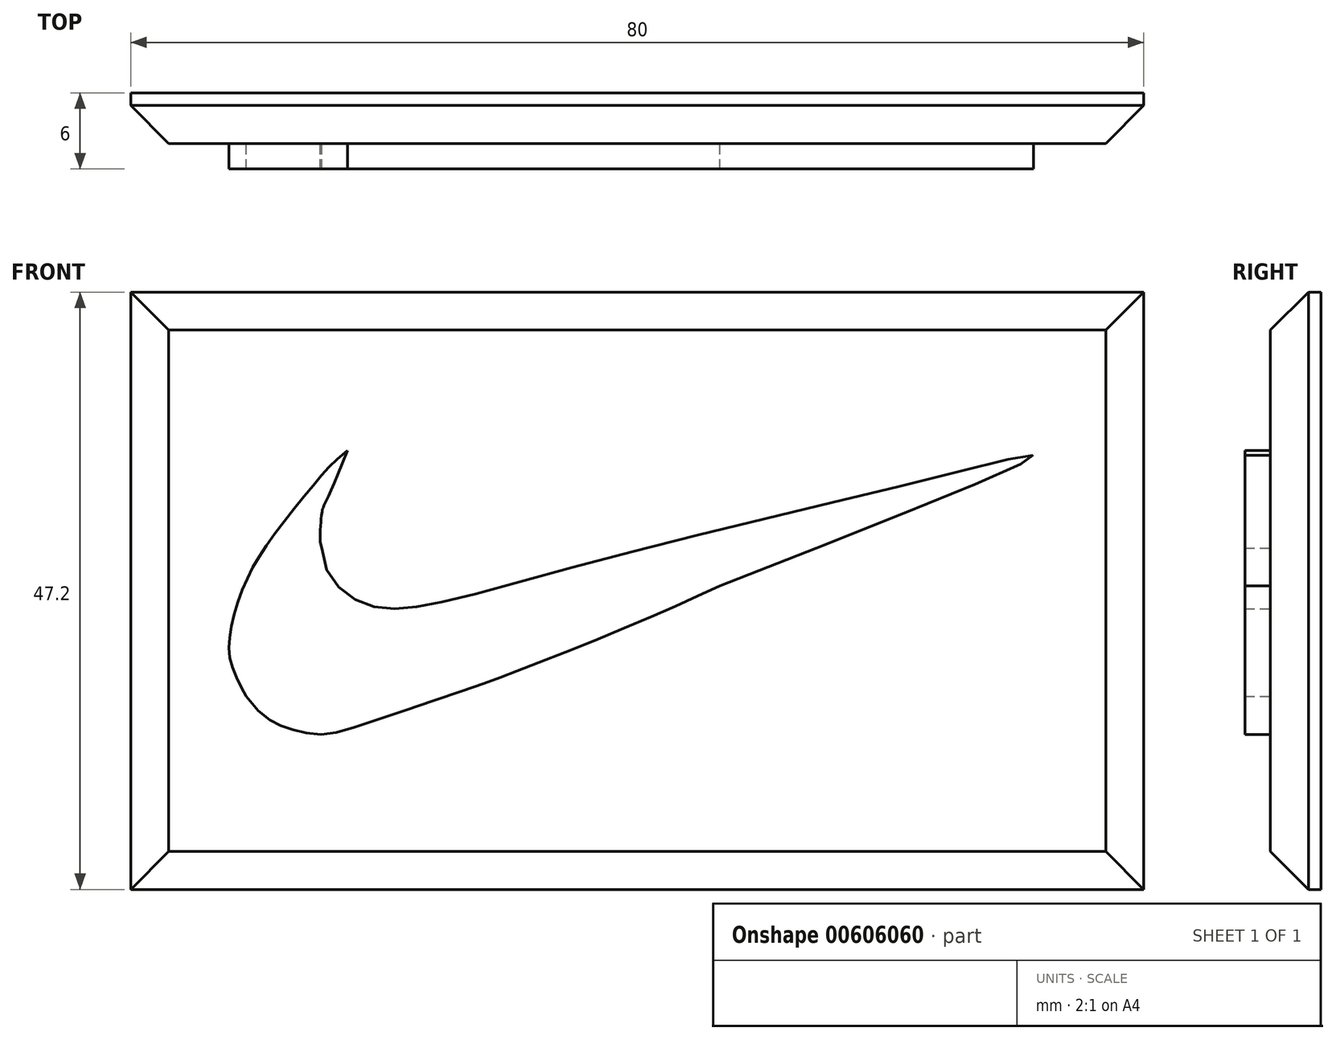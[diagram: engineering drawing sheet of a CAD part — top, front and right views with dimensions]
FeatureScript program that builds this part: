
annotation { "Feature Type Name" : "Feature", "Feature Type Description" : "" }
export const myFeature = defineFeature(function(context is Context, id is Id, definition is map)
    precondition{}
    {
        {
            var Q0;
            Q0=qCreatedBy(makeId("Front.planeOp"),FACE);
            var sketch = newSketch(context, id + "F0", { "sketchPlane" : qUnion([Q0])});
            skFitSpline(sketch, "E0", {"points": [v(17.14, 34.69) * mm, v(14.54, 32.1) * mm, v(10.96, 27.54) * mm, v(8.96, 24.03) * mm, v(7.87, 20.3) * mm, v(7.95, 17.78) * mm, v(9.12, 15.27) * mm], "startDerivative": vector(-21.1, -15.82) * mm, "endDerivative": vector(8.48, -15.2) * mm});
            skFitSpline(sketch, "E1", {"points": [v(9.12, 15.27) * mm, v(11.22, 13.25) * mm, v(12.83, 12.62) * mm, v(15.06, 12.25) * mm, v(18.78, 13.17) * mm, v(27.33, 16.1) * mm, v(30.87, 17.4) * mm, v(39.8, 21) * mm, v(46.54, 23.98) * mm], "startDerivative": vector(23.06, -33.31) * mm, "endDerivative": vector(41.07, 18.62) * mm});
            skFitSpline(sketch, "E2", {"points": [v(46.54, 23.98) * mm, v(71.28, 34.24) * mm, v(63.68, 32.6) * mm, v(39.66, 26.71) * mm, v(25.82, 23) * mm, v(22.02, 22.27) * mm, v(19.58, 22.27) * mm, v(17.57, 23) * mm, v(15.86, 24.59) * mm, v(15.08, 26.97) * mm], "startDerivative": vector(177.34, 69.63) * mm, "endDerivative": vector(-1.94, 45.8) * mm});
            skFitSpline(sketch, "E3", {"points": [v(15.08, 26.97) * mm, v(15.08, 29.62) * mm, v(17.14, 34.69) * mm], "startDerivative": vector(-1.73, 4.94) * mm, "endDerivative": vector(10.47, 25.79) * mm});
            skLineSegment(sketch, "E4.bottom", {"start": v(0, 47.2) * mm, "end": v(80, 47.2) * mm});
            skLineSegment(sketch, "E4.top", {"start": v(0, 0) * mm, "end": v(80, 0) * mm});
            skLineSegment(sketch, "E4.left", {"start": v(0, 47.2) * mm, "end": v(0, 0) * mm});
            skLineSegment(sketch, "E4.right", {"start": v(80, 47.2) * mm, "end": v(80, 0) * mm});
            skSolve(sketch);
        }
        {
            var Q0;
            Q0 = qSketchRegion(id + "F0", true);
            extrude(context, id + "F1", {"entities" : qUnion([Q0]), "depth" : 4 * mm, "offsetDistance" : 25 * mm});
        }
        {
            var Q0;
            Q0=makeQuery(id+"F0.imprint","IMPRINT",FACE,{"disambiguationData":[TD([[makeQuery(id+"F0.imprint","IMPRINT",EDGE,{"derivedFrom":sQuery(id+"F0.wireOp",EDGE,"E0")}),1.0]])]});
            extrude(context, id + "F2", {"entities" : qUnion([Q0]), "operationType" : NewBodyOperationType.ADD, "depth" : 6 * mm, "offsetDistance" : 25 * mm});
        }
        {
            var Q0;
            Q0=makeQuery(id+"F1.opExtrude","CAP_EDGE",EDGE,{"disambiguationData":[OSD([sQuery(id+"F0.wireOp",EDGE,"E4.left")])],"isStart":false});
            var Q1;
            Q1=makeQuery(id+"F1.opExtrude","CAP_EDGE",EDGE,{"disambiguationData":[OSD([sQuery(id+"F0.wireOp",EDGE,"E4.top")])],"isStart":false});
            var Q2;
            Q2=makeQuery(id+"F1.opExtrude","CAP_EDGE",EDGE,{"disambiguationData":[OSD([sQuery(id+"F0.wireOp",EDGE,"E4.right")])],"isStart":false});
            var Q3;
            Q3=makeQuery(id+"F1.opExtrude","CAP_EDGE",EDGE,{"disambiguationData":[OSD([sQuery(id+"F0.wireOp",EDGE,"E4.bottom")])],"isStart":false});
            chamfer(context, id + "F3", {"entities" : qUnion([Q0, Q1, Q2, Q3]), "width" : 3 * mm, "tangentPropagation" : true});
        }
    });
